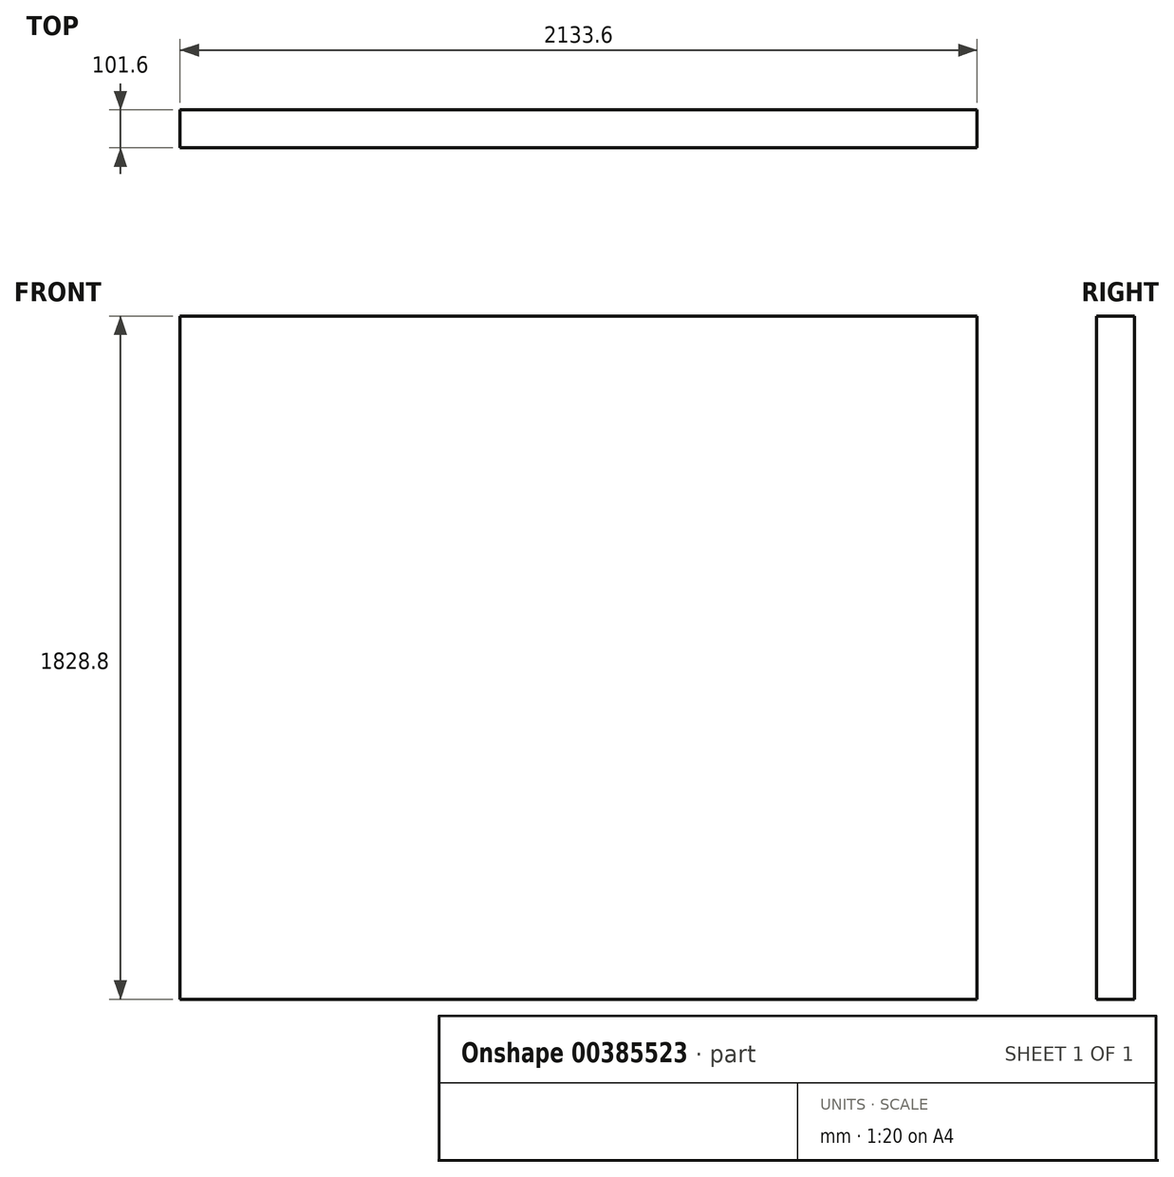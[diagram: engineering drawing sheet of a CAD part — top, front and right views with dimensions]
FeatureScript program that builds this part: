
annotation { "Feature Type Name" : "Feature", "Feature Type Description" : "" }
export const myFeature = defineFeature(function(context is Context, id is Id, definition is map)
    precondition{}
    {
        {
            var Q0;
            Q0=qCreatedBy(makeId("Front.planeOp"),FACE);
            var sketch = newSketch(context, id + "F0", { "sketchPlane" : qUnion([Q0])});
            skLineSegment(sketch, "E0.bottom", {"start": v(-1069.87, 914.4) * mm, "end": v(1063.73, 914.4) * mm});
            skLineSegment(sketch, "E0.top", {"start": v(-1069.87, -914.4) * mm, "end": v(1063.73, -914.4) * mm});
            skLineSegment(sketch, "E0.left", {"start": v(-1069.87, 914.4) * mm, "end": v(-1069.87, -914.4) * mm});
            skLineSegment(sketch, "E0.right", {"start": v(1063.73, 914.4) * mm, "end": v(1063.73, -914.4) * mm});
            skPoint(sketch, "E0.middle", {"position": v(-3.07, 0) * mm});
            skSolve(sketch);
        }
        {
            var Q0;
            Q0=makeQuery(id+"F0.imprint","IMPRINT",FACE,{"disambiguationData":[TD([[makeQuery(id+"F0.imprint","IMPRINT",EDGE,{"derivedFrom":sQuery(id+"F0.wireOp",EDGE,"E0.bottom")}),-1.0]])]});
            extrude(context, id + "F1", {"entities" : qUnion([Q0]), "depth" : 101.6 * mm});
        }
    });
